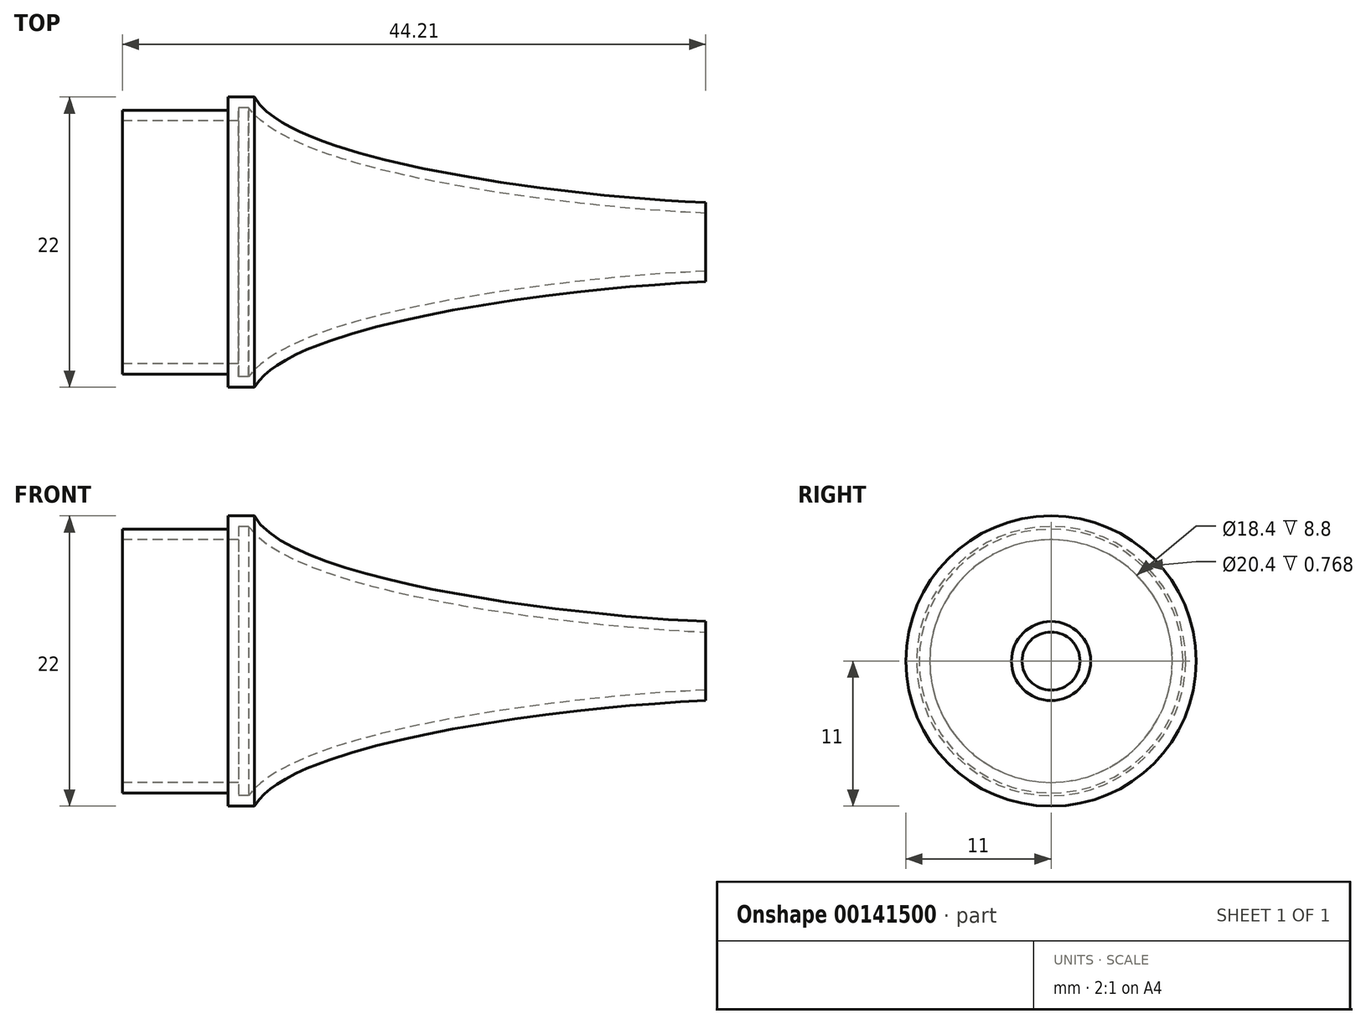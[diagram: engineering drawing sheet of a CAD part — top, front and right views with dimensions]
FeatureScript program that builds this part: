
annotation { "Feature Type Name" : "Feature", "Feature Type Description" : "" }
export const myFeature = defineFeature(function(context is Context, id is Id, definition is map)
    precondition{}
    {
        {
            var Q0;
            Q0=qCreatedBy(makeId("Front.planeOp"),FACE);
            var sketch = newSketch(context, id + "F0", { "sketchPlane" : qUnion([Q0])});
            skLineSegment(sketch, "E0", {"start": v(-17.33, 0) * mm, "end": v(17.67, 0) * mm, "construction": true});
            skLineSegment(sketch, "E1", {"start": v(0, 10) * mm, "end": v(8, 10) * mm});
            skLineSegment(sketch, "E2", {"start": v(8, 10) * mm, "end": v(8, 11) * mm});
            skLineSegment(sketch, "E3", {"start": v(8, 11) * mm, "end": v(10, 11) * mm});
            skLineSegment(sketch, "E4", {"start": v(0, 10) * mm, "end": v(0, 0) * mm});
            skLineSegment(sketch, "E5", {"start": v(0, 0) * mm, "end": v(44.2, 0) * mm});
            skLineSegment(sketch, "E6", {"start": v(44.2, 0) * mm, "end": v(44.2, 3) * mm});
            skFitSpline(sketch, "E7", {"points": [v(10, 11) * mm, v(44.2, 3) * mm], "startDerivative": vector(8.53, -15.09) * mm, "endDerivative": vector(29.74, -1.22) * mm});
            skSolve(sketch);
        }
        {
            var Q0;
            Q0 = qSketchRegion(id + "F0", true);
            var Q1;
            Q1=sQuery(id+"F0.wireOp",EDGE,"E0");
            revolve(context, id + "F1", {"entities" : qUnion([Q0]), "axis" : qUnion([Q1]), "revolveType" : RevolveType.FULL});
        }
        {
            var Q0;
            Q0=makeQuery(id+"F1.opRevolve","SWEPT_FACE",FACE,{"disambiguationData":[OSD([sQuery(id+"F0.wireOp",EDGE,"E4")])]});
            var Q1;
            Q1=makeQuery(id+"F1.opRevolve","SWEPT_FACE",FACE,{"disambiguationData":[OSD([sQuery(id+"F0.wireOp",EDGE,"E6")])]});
            var Q2;
            Q2=makeQuery(id+"F1.opRevolve","SWEPT_BODY",BODY,{"disambiguationData":[OSD([sQuery(id+"F0.wireOp",EDGE,"E1"),sQuery(id+"F0.wireOp",EDGE,"E2"),sQuery(id+"F0.wireOp",EDGE,"E3"),sQuery(id+"F0.wireOp",EDGE,"E4"),sQuery(id+"F0.wireOp",EDGE,"E5"),sQuery(id+"F0.wireOp",EDGE,"E6"),sQuery(id+"F0.wireOp",EDGE,"E7")])]});
            shell(context, id + "F2", {"entities" : qUnion([Q0, Q1]), "parts" : qUnion([Q2]), "thickness" : .8 * mm});
        }
    });
